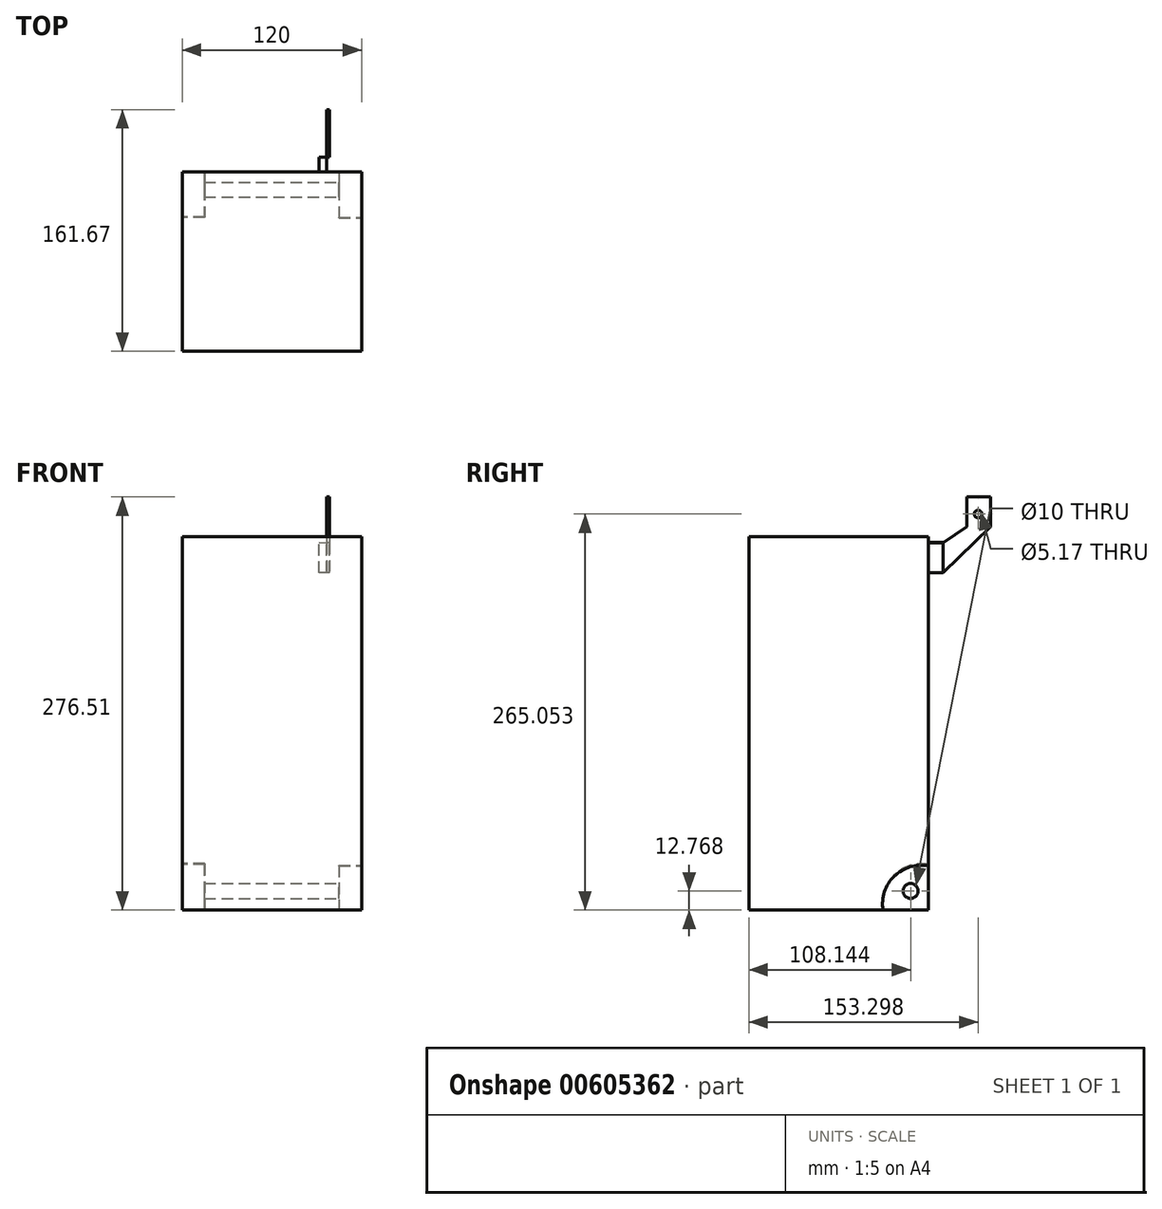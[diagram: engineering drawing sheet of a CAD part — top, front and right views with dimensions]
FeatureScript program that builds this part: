
annotation { "Feature Type Name" : "Feature", "Feature Type Description" : "" }
export const myFeature = defineFeature(function(context is Context, id is Id, definition is map)
    precondition{}
    {
        {
            var Q0;
            Q0=qCreatedBy(makeId("Top.planeOp"),FACE);
            var sketch = newSketch(context, id + "F0", { "sketchPlane" : qUnion([Q0])});
            skLineSegment(sketch, "E0.bottom", {"start": v(-96.54, 101.72) * mm, "end": v(23.46, 101.72) * mm});
            skLineSegment(sketch, "E0.top", {"start": v(-96.54, -18.28) * mm, "end": v(23.46, -18.28) * mm});
            skLineSegment(sketch, "E0.left", {"start": v(-96.54, 101.72) * mm, "end": v(-96.54, -18.28) * mm});
            skLineSegment(sketch, "E0.right", {"start": v(23.46, 101.72) * mm, "end": v(23.46, -18.28) * mm});
            skSolve(sketch);
        }
        {
            var Q0;
            Q0=makeQuery(id+"F0.imprint","IMPRINT",FACE,{"disambiguationData":[TD([[makeQuery(id+"F0.imprint","IMPRINT",EDGE,{"derivedFrom":sQuery(id+"F0.wireOp",EDGE,"E0.bottom")}),-1.0]])]});
            extrude(context, id + "F1", {"entities" : qUnion([Q0]), "depth" : 250 * mm, "offsetDistance" : 25 * mm});
        }
        {
            var Q0;
            Q0=makeQuery(id+"F1.opExtrude","SWEPT_FACE",FACE,{"disambiguationData":[OSD([sQuery(id+"F0.wireOp",EDGE,"E0.right")])]});
            var sketch = newSketch(context, id + "F2", { "sketchPlane" : qUnion([Q0])});
            skArc(sketch, "E1", {"start": v(101.72, 29.54) * mm, "mid": v(78.92, 22.6) * mm, "end": v(71.36, 0) * mm});
            skSolve(sketch);
        }
        {
            var Q0;
            Q0=makeQuery(id+"F1.opExtrude","SWEPT_FACE",FACE,{"disambiguationData":[OSD([sQuery(id+"F0.wireOp",EDGE,"E0.left")])]});
            var sketch = newSketch(context, id + "F3", { "sketchPlane" : qUnion([Q0])});
            skArc(sketch, "E2", {"start": v(-71.68, 0) * mm, "mid": v(-78.64, 23.22) * mm, "end": v(-101.72, 30.62) * mm});
            skSolve(sketch);
        }
        {
            var Q0;
            {var subQ0=sQuery(id+"F3.wireOp",EDGE,"E2");Q0=makeQuery(id+"F3.imprint","IMPRINT",FACE,{"disambiguationData":[TD([[makeQuery(id+"F3.imprint","IMPRINT",EDGE,{"derivedFrom":subQ0}),1.0]])]});}
            extrude(context, id + "F4", {"entities" : qUnion([Q0]), "operationType" : NewBodyOperationType.REMOVE, "oppositeDirection" : true, "depth" : 15 * mm, "offsetDistance" : 25 * mm});
        }
        {
            var Q0;
            {var subQ0=sQuery(id+"F2.wireOp",EDGE,"E1");Q0=makeQuery(id+"F2.imprint","IMPRINT",FACE,{"disambiguationData":[TD([[makeQuery(id+"F2.imprint","IMPRINT",EDGE,{"derivedFrom":subQ0}),1.0]])]});}
            extrude(context, id + "F5", {"entities" : qUnion([Q0]), "operationType" : NewBodyOperationType.REMOVE, "oppositeDirection" : true, "depth" : 15 * mm, "offsetDistance" : 25 * mm});
        }
        {
            var Q0;
            Q0=makeQuery(id+"F5.boolean.opBoolean","COPY",FACE,{"derivedFrom":makeQuery(id+"F5.opExtrude","CAP_FACE",FACE,{"disambiguationData":[OSD([sQuery(id+"F0.wireOp",EDGE,"E0.bottom"),sQuery(id+"F0.wireOp",EDGE,"E0.right"),sQuery(id+"F2.wireOp",EDGE,"E1")])],"isStart":false})});
            var sketch = newSketch(context, id + "F6", { "sketchPlane" : qUnion([Q0])});
            skCircle(sketch, "E3", {"center": v(89.86, 12.77) * mm, "radius": 5 * mm});
            skSolve(sketch);
        }
        {
            var Q0;
            Q0=makeQuery(id+"F6.imprint","IMPRINT",FACE,{"disambiguationData":[TD([[makeQuery(id+"F6.imprint","IMPRINT",EDGE,{"derivedFrom":sQuery(id+"F6.wireOp",EDGE,"E3")}),1.0]])]});
            extrude(context, id + "F7", {"entities" : qUnion([Q0]), "operationType" : NewBodyOperationType.REMOVE, "oppositeDirection" : true, "depth" : 90 * mm, "offsetDistance" : 25 * mm});
        }
        {
            var Q0;
            Q0=makeQuery(id+"F1.opExtrude","CAP_FACE",FACE,{"disambiguationData":[OSD([sQuery(id+"F0.wireOp",EDGE,"E0.bottom"),sQuery(id+"F0.wireOp",EDGE,"E0.top"),sQuery(id+"F0.wireOp",EDGE,"E0.left"),sQuery(id+"F0.wireOp",EDGE,"E0.right")])],"isStart":false});
            var sketch = newSketch(context, id + "F8", { "sketchPlane" : qUnion([Q0])});
            skLineSegment(sketch, "E4", {"start": v(-86.54, 91.72) * mm, "end": v(13.46, 91.72) * mm});
            skLineSegment(sketch, "E5", {"start": v(13.46, 91.72) * mm, "end": v(13.46, -8.28) * mm});
            skLineSegment(sketch, "E6", {"start": v(13.46, -8.28) * mm, "end": v(-86.54, -8.28) * mm});
            skLineSegment(sketch, "E7", {"start": v(-86.54, -8.28) * mm, "end": v(-86.54, 91.72) * mm});
            skSolve(sketch);
        }
        {
            var Q0;
            Q0=makeQuery(id+"F8.imprint","IMPRINT",FACE,{"disambiguationData":[TD([[makeQuery(id+"F8.imprint","IMPRINT",EDGE,{"derivedFrom":sQuery(id+"F8.wireOp",EDGE,"E4")}),-1.0]])]});
            var Q1;
            Q1=sQuery(id+"F8.wireOp",EDGE,"E5");
            var Q2;
            Q2=sQuery(id+"F8.wireOp",EDGE,"E6");
            var Q3;
            Q3=sQuery(id+"F8.wireOp",EDGE,"E7");
            var Q4;
            Q4=sQuery(id+"F8.wireOp",EDGE,"E4");
            extrude(context, id + "F9", {"entities" : qUnion([Q0]), "bodyType" : ToolBodyType.SURFACE, "surfaceEntities" : qUnion([Q1, Q2, Q3, Q4]), "depth" : 5 * mm, "offsetDistance" : 25 * mm});
        }
        {
            var Q0;
            Q0=makeQuery(id+"F1.opExtrude","SWEPT_FACE",FACE,{"disambiguationData":[OSD([sQuery(id+"F0.wireOp",EDGE,"E0.bottom")])]});
            var sketch = newSketch(context, id + "F10", { "sketchPlane" : qUnion([Q0])});
            skLineSegment(sketch, "E8", {"start": v(0, 245.66) * mm, "end": v(0, 225.83) * mm});
            skLineSegment(sketch, "E9", {"start": v(0, 225.83) * mm, "end": v(5.02, 225.83) * mm});
            skLineSegment(sketch, "E10", {"start": v(5.02, 225.83) * mm, "end": v(5.02, 246.1) * mm});
            skLineSegment(sketch, "E11", {"start": v(5.02, 246.1) * mm, "end": v(0, 245.66) * mm});
            skSolve(sketch);
        }
        {
            var Q0;
            Q0 = qSketchRegion(id + "F10", true);
            extrude(context, id + "F11", {"entities" : qUnion([Q0]), "operationType" : NewBodyOperationType.ADD, "depth" : 10 * mm, "offsetDistance" : 25 * mm});
        }
        {
            var Q0;
            Q0=makeQuery(id+"F11.opExtrude","SWEPT_FACE",FACE,{"disambiguationData":[OSD([sQuery(id+"F10.wireOp",EDGE,"E8")])]});
            var sketch = newSketch(context, id + "F12", { "sketchPlane" : qUnion([Q0])});
            skLineSegment(sketch, "E12", {"start": v(111.72, 225.83) * mm, "end": v(143.4, 256.68) * mm});
            skLineSegment(sketch, "E13", {"start": v(143.4, 256.68) * mm, "end": v(143.4, 276.51) * mm});
            skLineSegment(sketch, "E14", {"start": v(143.4, 276.51) * mm, "end": v(127.53, 276.51) * mm});
            skLineSegment(sketch, "E15", {"start": v(127.53, 276.51) * mm, "end": v(127.53, 256.68) * mm});
            skLineSegment(sketch, "E16", {"start": v(127.53, 256.68) * mm, "end": v(111.72, 245.66) * mm});
            skCircle(sketch, "E17", {"center": v(135.02, 265.05) * mm, "radius": 2.58 * mm});
            skSolve(sketch);
        }
        {
            var Q0;
            Q0=makeQuery(id+"F12.imprint","IMPRINT",FACE,{"disambiguationData":[TD([[makeQuery(id+"F12.imprint","IMPRINT",EDGE,{"derivedFrom":sQuery(id+"F12.wireOp",EDGE,"E12")}),1.0]])]});
            extrude(context, id + "F13", {"entities" : qUnion([Q0]), "depth" : 2 * mm, "offsetDistance" : 25 * mm});
        }
    });
